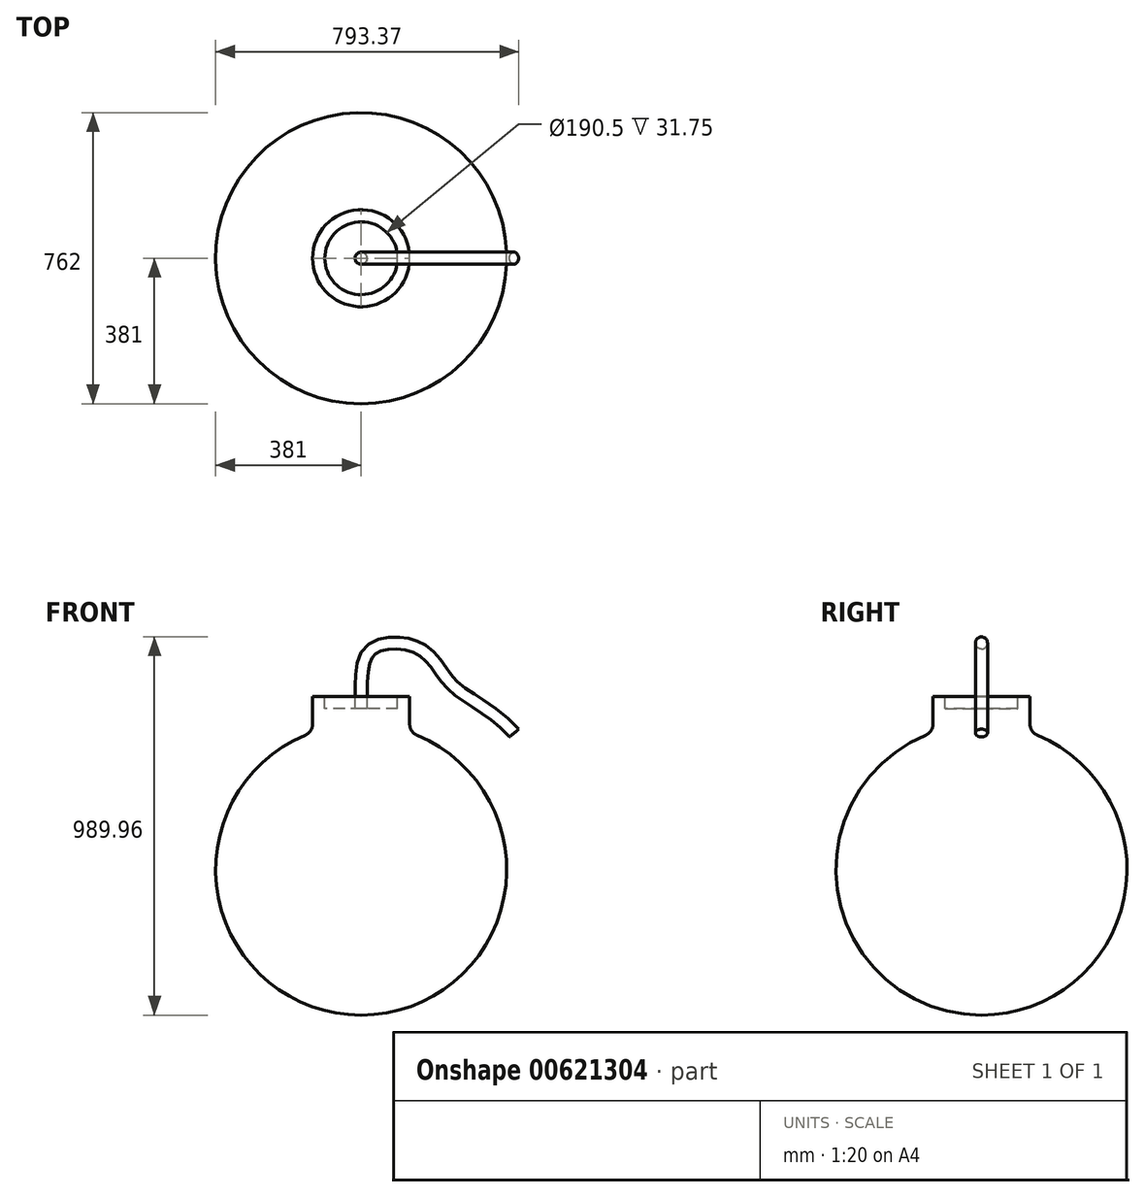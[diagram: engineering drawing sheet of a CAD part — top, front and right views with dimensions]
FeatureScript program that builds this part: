
annotation { "Feature Type Name" : "Feature", "Feature Type Description" : "" }
export const myFeature = defineFeature(function(context is Context, id is Id, definition is map)
    precondition{}
    {
        {
            var Q0;
            Q0=qCreatedBy(makeId("Right.planeOp"),FACE);
            var sketch = newSketch(context, id + "F0", { "sketchPlane" : qUnion([Q0])});
            skArc(sketch, "E0", {"start": v(0, 38.1) * mm, "mid": v(-38.1, 0) * mm, "end": v(0, -38.1) * mm});
            skLineSegment(sketch, "E1", {"start": v(0, 64.9) * mm, "end": v(0, -66.83) * mm});
            skSolve(sketch);
        }
        {
            var Q0;
            {var subQ0=sQuery(id+"F0.wireOp",EDGE,"E0");Q0=makeQuery(id+"F0.imprint","IMPRINT",FACE,{"disambiguationData":[TD([[makeQuery(id+"F0.imprint","IMPRINT",EDGE,{"derivedFrom":subQ0}),1.0]])]});}
            var Q1;
            Q1=sQuery(id+"F0.wireOp",EDGE,"E1");
            revolve(context, id + "F1", {"entities" : qUnion([Q0]), "axis" : qUnion([Q1]), "revolveType" : RevolveType.FULL, "oppositeDirection" : true});
        }
        {
            var Q0;
            Q0=qCreatedBy(makeId("Top.planeOp"),FACE);
            var sketch = newSketch(context, id + "F2", { "sketchPlane" : qUnion([Q0])});
            skCircle(sketch, "E2", {"center": v(0, 0) * mm, "radius": 12.7 * mm});
            skSolve(sketch);
        }
        {
            var Q0;
            Q0=qSketchRegion(id+"F2",true);
            extrude(context, id + "F3", {"entities" : qUnion([Q0]), "operationType" : NewBodyOperationType.ADD, "depth" : 45.35 * mm});
        }
        {
            var Q0;
            Q0=makeQuery(id+"F3.opExtrude","CAP_FACE",FACE,{"disambiguationData":[OSD([sQuery(id+"F2.wireOp",EDGE,"E2")])],"isStart":false});
            var sketch = newSketch(context, id + "F4", { "sketchPlane" : qUnion([Q0])});
            skCircle(sketch, "E3", {"center": v(0, 0) * mm, "radius": 9.53 * mm});
            skSolve(sketch);
        }
        {
            var Q0;
            Q0=qSketchRegion(id+"F4",true);
            extrude(context, id + "F5", {"entities" : qUnion([Q0]), "operationType" : NewBodyOperationType.REMOVE, "oppositeDirection" : true, "depth" : 3.17 * mm});
        }
        {
            var Q0;
            Q0=makeQuery(id+"F3.boolean.opBoolean","INTERSECT",EDGE,{"derivedFrom":[makeQuery(id+"F1.opRevolve","SWEPT_FACE",FACE,{"disambiguationData":[OSD([sQuery(id+"F0.wireOp",EDGE,"E0")])]}),makeQuery(id+"F3.opExtrude","SWEPT_FACE",FACE,{"disambiguationData":[OSD([sQuery(id+"F2.wireOp",EDGE,"E2")])]})]});
            fillet(context, id + "F6", {"entities" : qUnion([Q0]), "radius" : 3.17 * mm, "allowEdgeOverflow" : false});
        }
        {
            var Q0;
            Q0=makeQuery(id+"F5.boolean.opBoolean","COPY",FACE,{"derivedFrom":makeQuery(id+"F5.opExtrude","CAP_FACE",FACE,{"disambiguationData":[OSD([sQuery(id+"F4.wireOp",EDGE,"E3")])],"isStart":false})});
            var sketch = newSketch(context, id + "F7", { "sketchPlane" : qUnion([Q0])});
            skCircle(sketch, "E4", {"center": v(0, 0) * mm, "radius": 1.59 * mm});
            skSolve(sketch);
        }
        {
            var Q0;
            Q0=qCreatedBy(makeId("Front.planeOp"),FACE);
            var sketch = newSketch(context, id + "F8", { "sketchPlane" : qUnion([Q0])});
            skFitSpline(sketch, "E5", {"points": [v(0, 37.45) * mm, v(3.28, 58.05) * mm, v(15.76, 57.55) * mm, v(23.92, 48.28) * mm, v(40.05, 35.75) * mm], "startDerivative": vector(0, 129.41) * mm, "endDerivative": vector(60.12, -69.23) * mm});
            skSolve(sketch);
        }
        {
            var Q0;
            Q0=makeQuery(id+"F7.imprint","IMPRINT",FACE,{"disambiguationData":[TD([[makeQuery(id+"F7.imprint","IMPRINT",EDGE,{"derivedFrom":sQuery(id+"F7.wireOp",EDGE,"E4")}),1.0]])]});
            var Q1;
            Q1=sQuery(id+"F8.wireOp",EDGE,"E5");
            sweep(context, id + "F9", {"operationType" : NewBodyOperationType.ADD, "profiles" : qUnion([Q0]), "path" : qUnion([Q1])});
        }
        {
            var Q0;
            Q0=makeQuery(id+"F1.opRevolve","SWEPT_BODY",BODY,{"disambiguationData":[OSD([sQuery(id+"F0.wireOp",EDGE,"E0"),sQuery(id+"F0.wireOp",EDGE,"E1")])]});
            var Q1;
            Q1=qCreatedBy(makeId("Origin.pointOp"),VERTEX);
            transform(context, id + "F10", {"entities" : qUnion([Q0]), "transformType" : TransformType.SCALE_UNIFORMLY, "scale" : 10, "scalePoint" : qUnion([Q1]), "makeCopy" : false});
        }
    });
